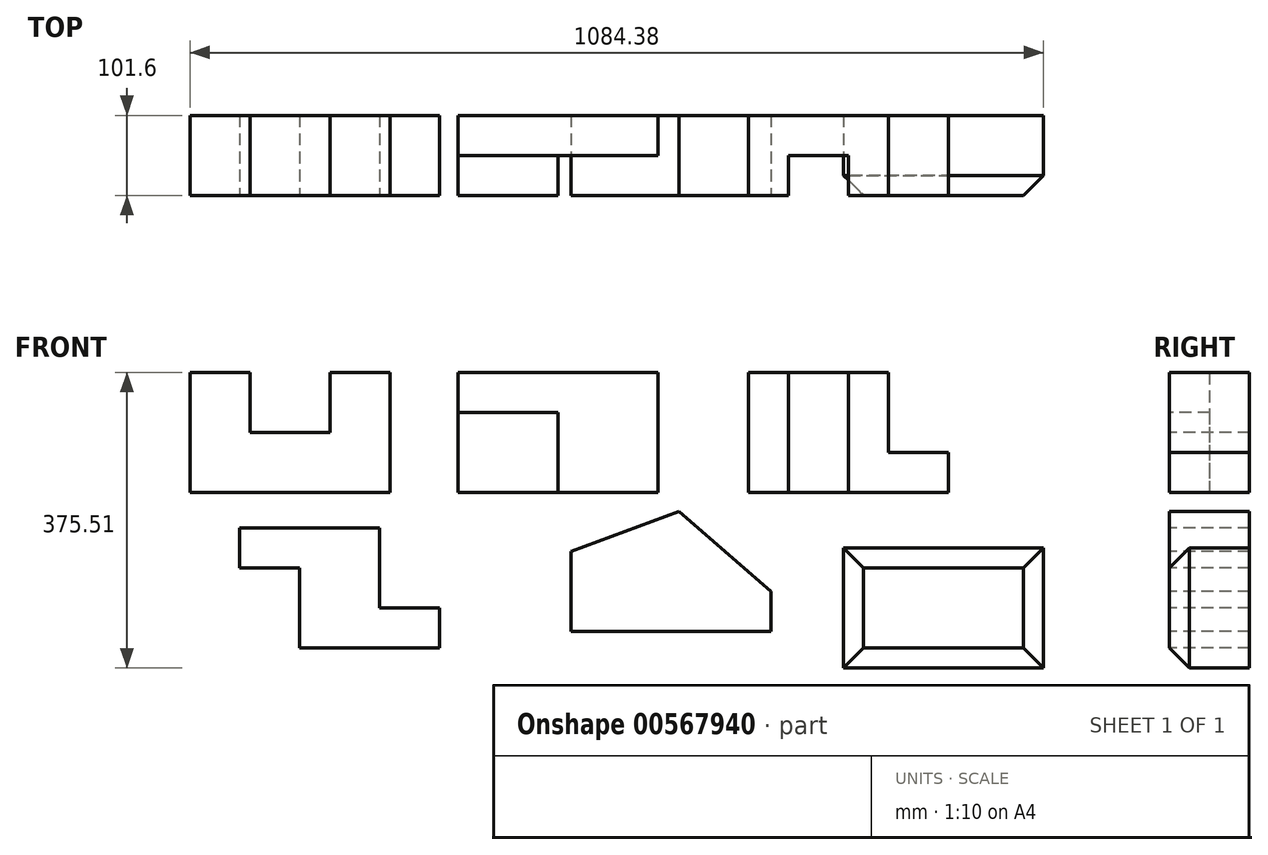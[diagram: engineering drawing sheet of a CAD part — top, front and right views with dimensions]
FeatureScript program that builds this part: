
annotation { "Feature Type Name" : "Feature", "Feature Type Description" : "" }
export const myFeature = defineFeature(function(context is Context, id is Id, definition is map)
    precondition{}
    {
        {
            var Q0;
            Q0=qCreatedBy(makeId("Front.planeOp"),FACE);
            var sketch = newSketch(context, id + "F0", { "sketchPlane" : qUnion([Q0])});
            skLineSegment(sketch, "E0", {"start": v(0, 0) * mm, "end": v(254, 0) * mm});
            skLineSegment(sketch, "E1", {"start": v(254, 0) * mm, "end": v(254, 152.4) * mm});
            skLineSegment(sketch, "E2", {"start": v(254, 152.4) * mm, "end": v(177.8, 152.4) * mm});
            skLineSegment(sketch, "E3", {"start": v(0, 0) * mm, "end": v(0, 152.4) * mm});
            skPoint(sketch, "E3.endSnap0", {"position": v(215.9, 152.4) * mm});
            skLineSegment(sketch, "E4", {"start": v(0, 152.4) * mm, "end": v(76.2, 152.4) * mm});
            skLineSegment(sketch, "E5", {"start": v(76.2, 152.4) * mm, "end": v(76.2, 76.2) * mm});
            skLineSegment(sketch, "E6", {"start": v(76.2, 76.2) * mm, "end": v(177.8, 76.2) * mm});
            skLineSegment(sketch, "E7", {"start": v(177.8, 76.2) * mm, "end": v(177.8, 152.4) * mm});
            skSolve(sketch);
        }
        {
            var Q0;
            Q0 = qSketchRegion(id + "F0", true);
            extrude(context, id + "F1", {"entities" : qUnion([Q0]), "oppositeDirection" : true, "depth" : 101.6 * mm, "offsetDistance" : 25.4 * mm});
        }
        {
            var Q0;
            Q0=qCreatedBy(makeId("Top.planeOp"),FACE);
            var sketch = newSketch(context, id + "F2", { "sketchPlane" : qUnion([Q0])});
            skLineSegment(sketch, "E8", {"start": v(340.42, 0) * mm, "end": v(340.42, 101.6) * mm});
            skLineSegment(sketch, "E9", {"start": v(340.42, 101.6) * mm, "end": v(594.42, 101.6) * mm});
            skLineSegment(sketch, "E10", {"start": v(594.42, 101.6) * mm, "end": v(594.42, 50.8) * mm});
            skLineSegment(sketch, "E11", {"start": v(594.42, 50.8) * mm, "end": v(467.42, 50.8) * mm});
            skLineSegment(sketch, "E12", {"start": v(467.42, 50.8) * mm, "end": v(467.42, 0) * mm});
            skLineSegment(sketch, "E13", {"start": v(467.42, 0) * mm, "end": v(340.42, 0) * mm});
            skSolve(sketch);
        }
        {
            var Q0;
            Q0=makeQuery(id+"F2.imprint","IMPRINT",FACE,{"disambiguationData":[TD([[makeQuery(id+"F2.imprint","IMPRINT",EDGE,{"derivedFrom":sQuery(id+"F2.wireOp",EDGE,"E8")}),-1.0]])]});
            extrude(context, id + "F3", {"entities" : qUnion([Q0]), "depth" : 152.4 * mm, "offsetDistance" : 25.4 * mm});
        }
        {
            var Q0;
            Q0=makeQuery(id+"F3.opExtrude","SWEPT_FACE",FACE,{"disambiguationData":[OSD([sQuery(id+"F2.wireOp",EDGE,"E13")])]});
            var sketch = newSketch(context, id + "F4", { "sketchPlane" : qUnion([Q0])});
            skLineSegment(sketch, "E14.bottom", {"start": v(340.42, 152.4) * mm, "end": v(467.42, 152.4) * mm});
            skLineSegment(sketch, "E14.top", {"start": v(340.42, 101.6) * mm, "end": v(467.42, 101.6) * mm});
            skLineSegment(sketch, "E14.left", {"start": v(340.42, 152.4) * mm, "end": v(340.42, 101.6) * mm});
            skLineSegment(sketch, "E14.right", {"start": v(467.42, 152.4) * mm, "end": v(467.42, 101.6) * mm});
            skSolve(sketch);
        }
        {
            var Q0;
            Q0 = qSketchRegion(id + "F4", true);
            extrude(context, id + "F5", {"entities" : qUnion([Q0]), "operationType" : NewBodyOperationType.REMOVE, "oppositeDirection" : true, "depth" : 50.8 * mm, "offsetDistance" : 25.4 * mm});
        }
        {
            var Q0;
            Q0=qCreatedBy(makeId("Front.planeOp"),FACE);
            var sketch = newSketch(context, id + "F6", { "sketchPlane" : qUnion([Q0])});
            skLineSegment(sketch, "E15", {"start": v(709.55, 152.4) * mm, "end": v(709.55, 0) * mm});
            skLineSegment(sketch, "E16", {"start": v(709.55, 0) * mm, "end": v(963.55, 0) * mm});
            skLineSegment(sketch, "E17", {"start": v(963.55, 0) * mm, "end": v(963.55, 50.8) * mm});
            skLineSegment(sketch, "E18", {"start": v(963.55, 50.8) * mm, "end": v(887.35, 50.8) * mm});
            skLineSegment(sketch, "E19", {"start": v(887.35, 50.8) * mm, "end": v(887.35, 152.4) * mm});
            skLineSegment(sketch, "E20", {"start": v(887.35, 152.4) * mm, "end": v(709.55, 152.4) * mm});
            skSolve(sketch);
        }
        {
            var Q0;
            Q0=makeQuery(id+"F6.imprint","IMPRINT",FACE,{"disambiguationData":[TD([[makeQuery(id+"F6.imprint","IMPRINT",EDGE,{"derivedFrom":sQuery(id+"F6.wireOp",EDGE,"E15")}),1.0]])]});
            extrude(context, id + "F7", {"entities" : qUnion([Q0]), "oppositeDirection" : true, "depth" : 101.6 * mm, "offsetDistance" : 25.4 * mm});
        }
        {
            var Q0;
            Q0=makeQuery(id+"F7.opExtrude","SWEPT_FACE",FACE,{"disambiguationData":[OSD([sQuery(id+"F6.wireOp",EDGE,"E20")])]});
            var sketch = newSketch(context, id + "F8", { "sketchPlane" : qUnion([Q0])});
            skLineSegment(sketch, "E21.bottom", {"start": v(760.35, 0) * mm, "end": v(836.55, 0) * mm});
            skLineSegment(sketch, "E21.top", {"start": v(760.35, 50.8) * mm, "end": v(836.55, 50.8) * mm});
            skLineSegment(sketch, "E21.left", {"start": v(760.35, 0) * mm, "end": v(760.35, 50.8) * mm});
            skLineSegment(sketch, "E21.right", {"start": v(836.55, 0) * mm, "end": v(836.55, 50.8) * mm});
            skSolve(sketch);
        }
        {
            var Q0;
            Q0=makeQuery(id+"F8.imprint","IMPRINT",FACE,{"disambiguationData":[TD([[makeQuery(id+"F8.imprint","IMPRINT",EDGE,{"derivedFrom":sQuery(id+"F8.wireOp",EDGE,"E21.bottom")}),-1.0]])]});
            extrude(context, id + "F9", {"entities" : qUnion([Q0]), "operationType" : NewBodyOperationType.REMOVE, "oppositeDirection" : true, "depth" : 152.4 * mm, "offsetDistance" : 25.4 * mm});
        }
        {
            var Q0;
            Q0=qCreatedBy(makeId("Front.planeOp"),FACE);
            var sketch = newSketch(context, id + "F10", { "sketchPlane" : qUnion([Q0])});
            skLineSegment(sketch, "E22", {"start": v(62.95, -45.25) * mm, "end": v(62.95, -96.05) * mm});
            skLineSegment(sketch, "E23", {"start": v(62.95, -96.05) * mm, "end": v(139.15, -96.05) * mm});
            skLineSegment(sketch, "E24", {"start": v(139.15, -96.05) * mm, "end": v(139.15, -197.65) * mm});
            skLineSegment(sketch, "E25", {"start": v(139.15, -197.65) * mm, "end": v(316.95, -197.65) * mm});
            skLineSegment(sketch, "E26", {"start": v(316.95, -197.65) * mm, "end": v(316.95, -146.85) * mm});
            skLineSegment(sketch, "E27", {"start": v(316.95, -146.85) * mm, "end": v(240.75, -146.85) * mm});
            skLineSegment(sketch, "E28", {"start": v(240.75, -146.85) * mm, "end": v(240.75, -45.25) * mm});
            skLineSegment(sketch, "E29", {"start": v(240.75, -45.25) * mm, "end": v(62.95, -45.25) * mm});
            skSolve(sketch);
        }
        {
            var Q0;
            Q0=makeQuery(id+"F10.imprint","IMPRINT",FACE,{"disambiguationData":[TD([[makeQuery(id+"F10.imprint","IMPRINT",EDGE,{"derivedFrom":sQuery(id+"F10.wireOp",EDGE,"E22")}),1.0]])]});
            extrude(context, id + "F11", {"entities" : qUnion([Q0]), "oppositeDirection" : true, "depth" : 101.6 * mm, "offsetDistance" : 25.4 * mm});
        }
        {
            var Q0;
            Q0=qCreatedBy(makeId("Front.planeOp"),FACE);
            var sketch = newSketch(context, id + "F12", { "sketchPlane" : qUnion([Q0])});
            skLineSegment(sketch, "E30", {"start": v(483.86, -176.72) * mm, "end": v(737.86, -176.72) * mm});
            skLineSegment(sketch, "E31", {"start": v(737.86, -176.72) * mm, "end": v(737.86, -125.92) * mm});
            skLineSegment(sketch, "E32", {"start": v(737.86, -125.92) * mm, "end": v(621.14, -24.32) * mm});
            skLineSegment(sketch, "E33", {"start": v(483.86, -176.72) * mm, "end": v(483.86, -75.12) * mm});
            skLineSegment(sketch, "E34", {"start": v(483.86, -75.12) * mm, "end": v(621.14, -24.32) * mm});
            skSolve(sketch);
        }
        {
            var Q0;
            Q0=makeQuery(id+"F12.imprint","IMPRINT",FACE,{"disambiguationData":[TD([[makeQuery(id+"F12.imprint","IMPRINT",EDGE,{"derivedFrom":sQuery(id+"F12.wireOp",EDGE,"E30")}),1.0]])]});
            extrude(context, id + "F13", {"entities" : qUnion([Q0]), "oppositeDirection" : true, "depth" : 101.6 * mm, "offsetDistance" : 25.4 * mm});
        }
        {
            var Q0;
            Q0=qCreatedBy(makeId("Front.planeOp"),FACE);
            var sketch = newSketch(context, id + "F14", { "sketchPlane" : qUnion([Q0])});
            skLineSegment(sketch, "E35", {"start": v(830.38, -70.7) * mm, "end": v(830.38, -223.1) * mm});
            skLineSegment(sketch, "E36", {"start": v(830.38, -223.1) * mm, "end": v(1084.38, -223.1) * mm});
            skLineSegment(sketch, "E37", {"start": v(1084.38, -223.1) * mm, "end": v(1084.38, -70.7) * mm});
            skLineSegment(sketch, "E38", {"start": v(1084.38, -70.7) * mm, "end": v(830.38, -70.7) * mm});
            skSolve(sketch);
        }
        {
            var Q0;
            Q0=makeQuery(id+"F14.imprint","IMPRINT",FACE,{"disambiguationData":[TD([[makeQuery(id+"F14.imprint","IMPRINT",EDGE,{"derivedFrom":sQuery(id+"F14.wireOp",EDGE,"E35")}),1.0]])]});
            extrude(context, id + "F15", {"entities" : qUnion([Q0]), "oppositeDirection" : true, "depth" : 101.6 * mm, "offsetDistance" : 25.4 * mm});
        }
        {
            var Q0;
            Q0=makeQuery(id+"F15.opExtrude","CAP_FACE",FACE,{"disambiguationData":[OSD([sQuery(id+"F14.wireOp",EDGE,"E35"),sQuery(id+"F14.wireOp",EDGE,"E36"),sQuery(id+"F14.wireOp",EDGE,"E37"),sQuery(id+"F14.wireOp",EDGE,"E38")])],"isStart":true});
            chamfer(context, id + "F16", {"entities" : qUnion([Q0]), "width" : 25.4 * mm, "tangentPropagation" : true});
        }
    });
